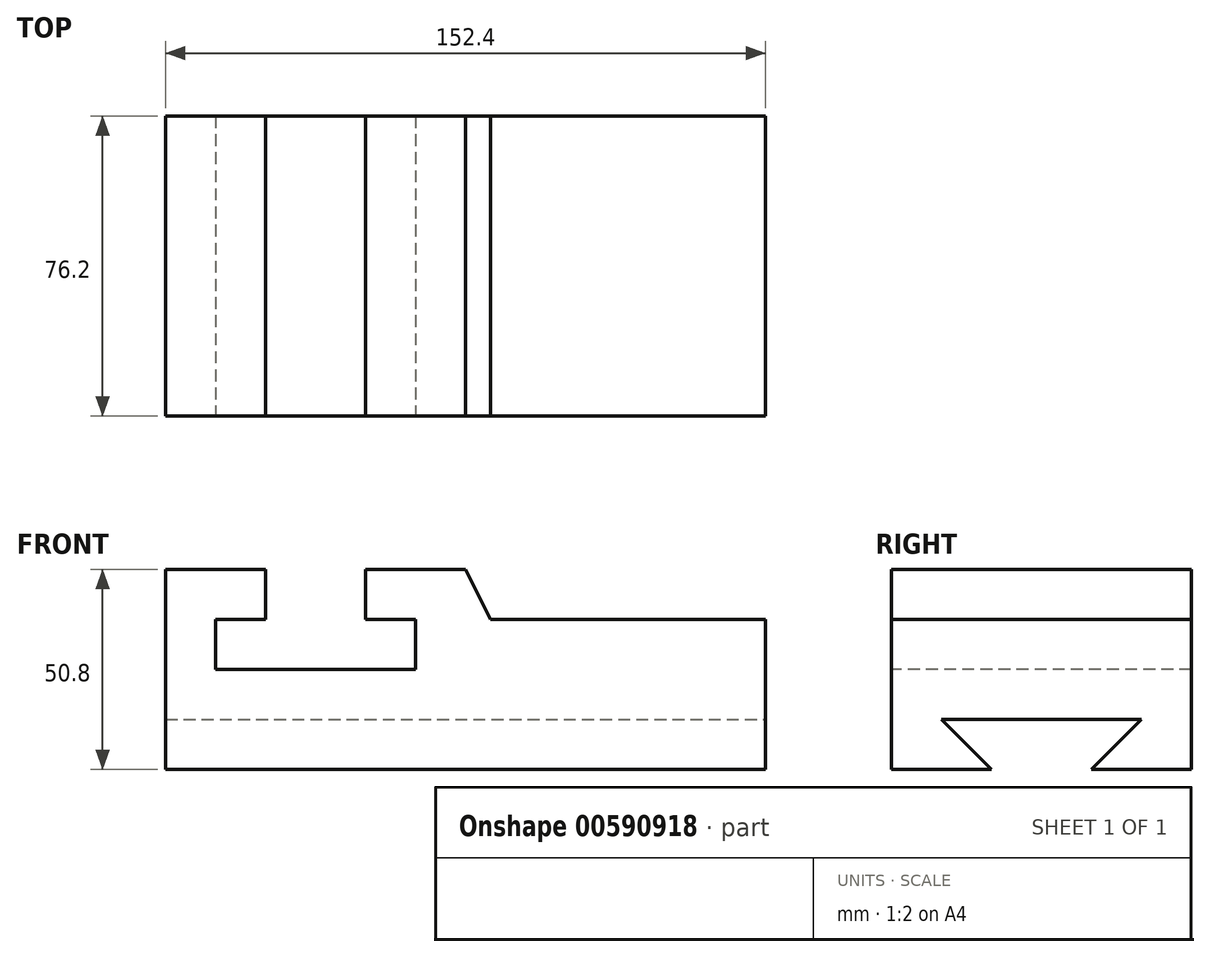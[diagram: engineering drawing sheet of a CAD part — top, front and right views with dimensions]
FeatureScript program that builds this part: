
annotation { "Feature Type Name" : "Feature", "Feature Type Description" : "" }
export const myFeature = defineFeature(function(context is Context, id is Id, definition is map)
    precondition{}
    {
        {
            var Q0;
            Q0=qCreatedBy(makeId("Front.planeOp"),FACE);
            var sketch = newSketch(context, id + "F0", { "sketchPlane" : qUnion([Q0])});
            skLineSegment(sketch, "E0.bottom", {"start": v(0, 0) * mm, "end": v(152.4, 0) * mm});
            skLineSegment(sketch, "E0.top", {"start": v(0, 50.8) * mm, "end": v(152.4, 50.8) * mm});
            skLineSegment(sketch, "E0.left", {"start": v(0, 0) * mm, "end": v(0, 50.8) * mm});
            skLineSegment(sketch, "E0.right", {"start": v(152.4, 0) * mm, "end": v(152.4, 50.8) * mm});
            skPoint(sketch, "E1", {"position": v(25.4, 50.8) * mm});
            skPoint(sketch, "E2", {"position": v(50.8, 50.8) * mm});
            skLineSegment(sketch, "E3", {"start": v(25.4, 50.8) * mm, "end": v(25.4, 38.1) * mm});
            skLineSegment(sketch, "E4", {"start": v(25.4, 38.1) * mm, "end": v(12.7, 38.1) * mm});
            skLineSegment(sketch, "E5", {"start": v(12.7, 38.1) * mm, "end": v(12.7, 25.4) * mm});
            skLineSegment(sketch, "E6", {"start": v(12.7, 25.4) * mm, "end": v(63.5, 25.4) * mm});
            skLineSegment(sketch, "E7", {"start": v(63.5, 25.4) * mm, "end": v(63.5, 38.1) * mm});
            skLineSegment(sketch, "E8", {"start": v(63.5, 38.1) * mm, "end": v(50.8, 38.1) * mm});
            skLineSegment(sketch, "E9", {"start": v(50.8, 38.1) * mm, "end": v(50.8, 50.8) * mm});
            skPoint(sketch, "E10", {"position": v(76.2, 50.8) * mm});
            skPoint(sketch, "E11", {"position": v(82.55, 50.8) * mm});
            skPoint(sketch, "E12", {"position": v(82.55, 38.1) * mm});
            skLineSegment(sketch, "E13", {"start": v(76.2, 50.8) * mm, "end": v(82.55, 38.1) * mm});
            skLineSegment(sketch, "E14", {"start": v(82.55, 38.1) * mm, "end": v(152.4, 38.1) * mm});
            skSolve(sketch);
        }
        {
            var Q0;
            {var subQ2=sQuery(id+"F0.wireOp",EDGE,"E0.bottom");Q0=makeQuery(id+"F0.imprint","IMPRINT",FACE,{"disambiguationData":[TD([[makeQuery(id+"F0.imprint","IMPRINT",EDGE,{"derivedFrom":subQ2}),1.0]])]});}
            extrude(context, id + "F1", {"entities" : qUnion([Q0]), "oppositeDirection" : true, "depth" : 76.2 * mm, "offsetDistance" : 25.4 * mm});
        }
        {
            var Q0;
            Q0=makeQuery(id+"F1.opExtrude","SWEPT_FACE",FACE,{"disambiguationData":[OSD([sQuery(id+"F0.wireOp",EDGE,"E0.right")])]});
            var sketch = newSketch(context, id + "F2", { "sketchPlane" : qUnion([Q0])});
            skPoint(sketch, "E15", {"position": v(50.8, 0) * mm});
            skPoint(sketch, "E16", {"position": v(25.4, 0) * mm});
            skPoint(sketch, "E17", {"position": v(12.7, 12.7) * mm});
            skPoint(sketch, "E18", {"position": v(63.5, 12.7) * mm});
            skLineSegment(sketch, "E19", {"start": v(25.4, 0) * mm, "end": v(12.7, 12.7) * mm});
            skLineSegment(sketch, "E20", {"start": v(50.8, 0) * mm, "end": v(63.5, 12.7) * mm});
            skLineSegment(sketch, "E21", {"start": v(12.7, 12.7) * mm, "end": v(63.5, 12.7) * mm});
            skSolve(sketch);
        }
        {
            var Q0;
            {var subQ0=sQuery(id+"F2.wireOp",EDGE,"E19");Q0=makeQuery(id+"F2.imprint","IMPRINT",FACE,{"disambiguationData":[TD([[makeQuery(id+"F2.imprint","IMPRINT",EDGE,{"derivedFrom":subQ0}),-1.0]])]});}
            extrude(context, id + "F3", {"entities" : qUnion([Q0]), "operationType" : NewBodyOperationType.REMOVE, "oppositeDirection" : true, "depth" : 152.4 * mm, "offsetDistance" : 25.4 * mm});
        }
    });
